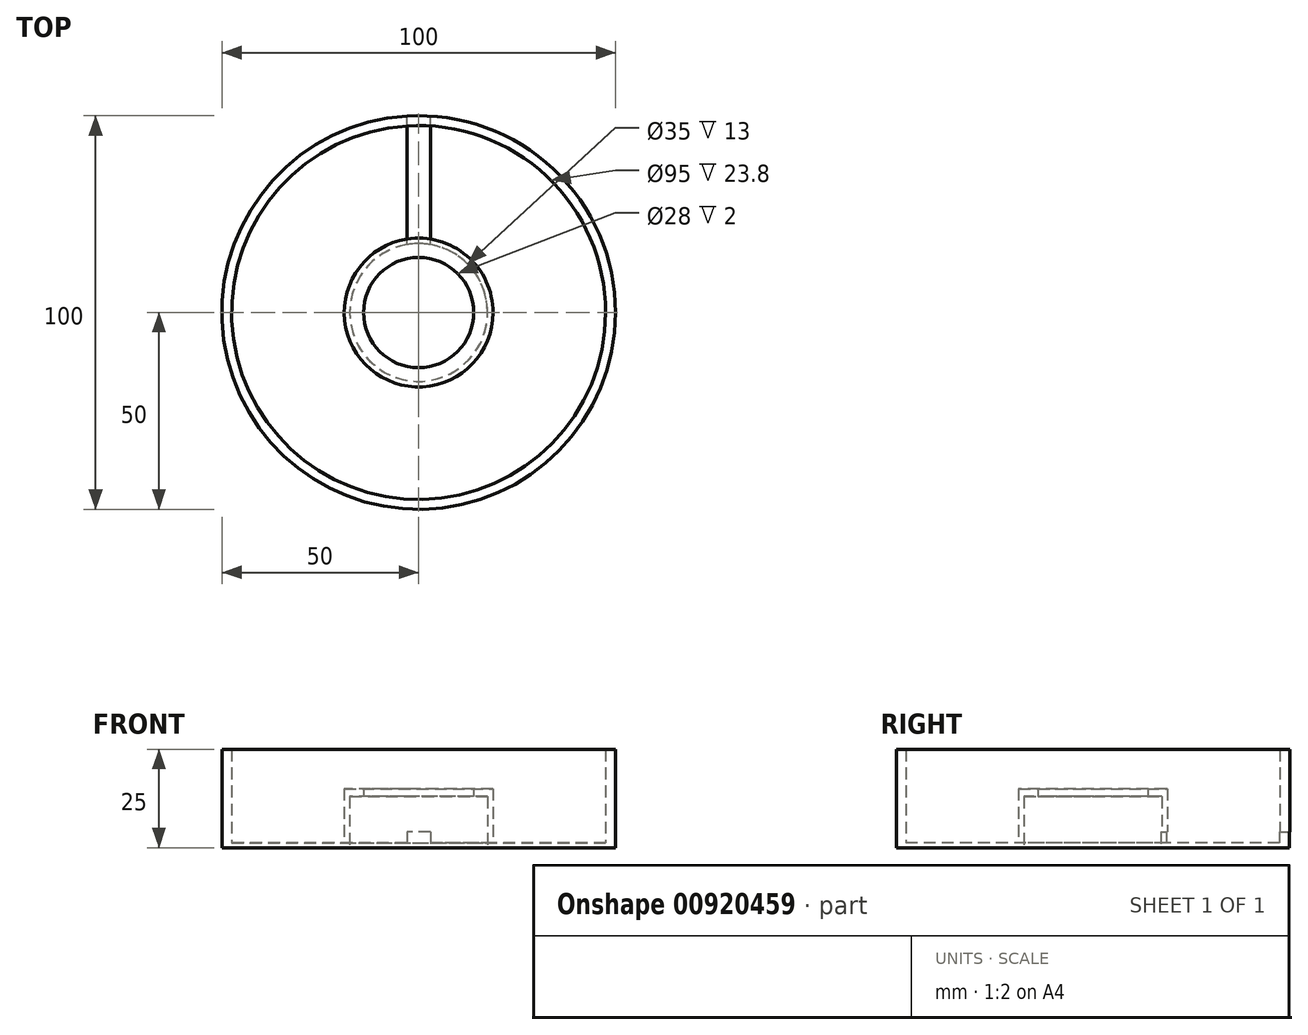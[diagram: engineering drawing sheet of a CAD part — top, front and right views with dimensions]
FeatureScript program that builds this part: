
annotation { "Feature Type Name" : "Feature", "Feature Type Description" : "" }
export const myFeature = defineFeature(function(context is Context, id is Id, definition is map)
    precondition{}
    {
        {
            var Q0;
            Q0=qCreatedBy(makeId("Top.planeOp"),FACE);
            var sketch = newSketch(context, id + "F0", { "sketchPlane" : qUnion([Q0])});
            skCircle(sketch, "E0", {"center": v(0, 0) * mm, "radius": 14 * mm});
            skCircle(sketch, "E1", {"center": v(0, 0) * mm, "radius": 17.5 * mm});
            skCircle(sketch, "E2", {"center": v(0, 0) * mm, "radius": 18.9 * mm});
            skCircle(sketch, "E3", {"center": v(0, 0) * mm, "radius": 50 * mm});
            skCircle(sketch, "E4", {"center": v(0, 0) * mm, "radius": 47.5 * mm});
            skLineSegment(sketch, "E5", {"start": v(0, 0) * mm, "end": v(3, 0) * mm});
            skLineSegment(sketch, "E6", {"start": v(0, -9.09) * mm, "end": v(0, 9.38) * mm, "construction": true});
            skLineSegment(sketch, "E7", {"start": v(3, 0) * mm, "end": v(3, 49.9) * mm});
            skLineSegment(sketch, "E8.MirrorCS", {"start": v(0, 0) * mm, "end": v(-3, 0) * mm});
            skLineSegment(sketch, "E9.MirrorCS", {"start": v(-3, 0) * mm, "end": v(-3, 49.9) * mm});
            skSolve(sketch);
        }
        {
            var Q0;
            Q0=makeQuery(id+"F0.imprint","IMPRINT",FACE,{"disambiguationData":[TD([[makeQuery(id+"F0.imprint","IMPRINT",EDGE,{"derivedFrom":sQuery(id+"F0.wireOp",EDGE,"E1")}),-1.0]])]});
            var Q1;
            Q1=makeQuery(id+"F0.imprint","IMPRINT",FACE,{"disambiguationData":[TD([[makeQuery(id+"F0.imprint","IMPRINT",EDGE,{"derivedFrom":sQuery(id+"F0.wireOp",EDGE,"E0")}),-1.0]])]});
            extrude(context, id + "F1", {"entities" : qUnion([Q0, Q1]), "depth" : 15 * mm, "offsetDistance" : 25 * mm});
        }
        {
            var Q0;
            Q0=makeQuery(id+"F0.imprint","IMPRINT",FACE,{"disambiguationData":[TD([[makeQuery(id+"F0.imprint","IMPRINT",EDGE,{"derivedFrom":sQuery(id+"F0.wireOp",EDGE,"E0")}),-1.0]])]});
            extrude(context, id + "F2", {"entities" : qUnion([Q0]), "operationType" : NewBodyOperationType.REMOVE, "depth" : 13 * mm, "offsetDistance" : 25 * mm});
        }
        {
            var Q0;
            Q0=makeQuery(id+"F0.imprint","IMPRINT",FACE,{"disambiguationData":[TD([[makeQuery(id+"F0.imprint","IMPRINT",EDGE,{"derivedFrom":sQuery(id+"F0.wireOp",EDGE,"E2")}),-1.0]])]});
            extrude(context, id + "F3", {"entities" : qUnion([Q0]), "operationType" : NewBodyOperationType.ADD, "depth" : 1.2 * mm, "offsetDistance" : 25 * mm});
        }
        {
            var Q0;
            Q0=makeQuery(id+"F0.imprint","IMPRINT",FACE,{"disambiguationData":[TD([[makeQuery(id+"F0.imprint","IMPRINT",EDGE,{"derivedFrom":sQuery(id+"F0.wireOp",EDGE,"E3")}),1.0]])]});
            extrude(context, id + "F4", {"entities" : qUnion([Q0]), "operationType" : NewBodyOperationType.ADD, "depth" : 25 * mm, "offsetDistance" : 25 * mm});
        }
        {
            var Q0;
            {var subQ0=sQuery(id+"F0.wireOp",EDGE,"E7");var subQ1=sQuery(id+"F0.wireOp",EDGE,"E1");var subQ2=makeQuery(id+"F0.imprint","INTERSECT",VERTEX,{"derivedFrom":[subQ1,subQ0]});Q0=makeQuery(id+"F0.imprint","IMPRINT",FACE,{"disambiguationData":[TD([[makeQuery(id+"F0.imprint","IMPRINT",EDGE,{"disambiguationData":[TD([[subQ2,-1.0]])],"derivedFrom":subQ1}),-1.0]])]});}
            var Q1;
            {var subQ0=sQuery(id+"F0.wireOp",EDGE,"E7");var subQ1=sQuery(id+"F0.wireOp",EDGE,"E2");var subQ2=makeQuery(id+"F0.imprint","INTERSECT",VERTEX,{"derivedFrom":[subQ1,subQ0]});Q1=makeQuery(id+"F0.imprint","IMPRINT",FACE,{"disambiguationData":[TD([[makeQuery(id+"F0.imprint","IMPRINT",EDGE,{"disambiguationData":[TD([[subQ2,-1.0]])],"derivedFrom":subQ1}),-1.0]])]});}
            var Q2;
            {var subQ0=sQuery(id+"F0.wireOp",EDGE,"E7");var subQ1=sQuery(id+"F0.wireOp",EDGE,"E3");var subQ2=makeQuery(id+"F0.imprint","INTERSECT",VERTEX,{"derivedFrom":[subQ1,subQ0]});Q2=makeQuery(id+"F0.imprint","IMPRINT",FACE,{"disambiguationData":[TD([[makeQuery(id+"F0.imprint","IMPRINT",EDGE,{"disambiguationData":[TD([[subQ2,-1.0]])],"derivedFrom":subQ1}),1.0]])]});}
            extrude(context, id + "F5", {"entities" : qUnion([Q0, Q1, Q2]), "operationType" : NewBodyOperationType.REMOVE, "depth" : 4 * mm, "offsetDistance" : 25 * mm});
        }
    });
